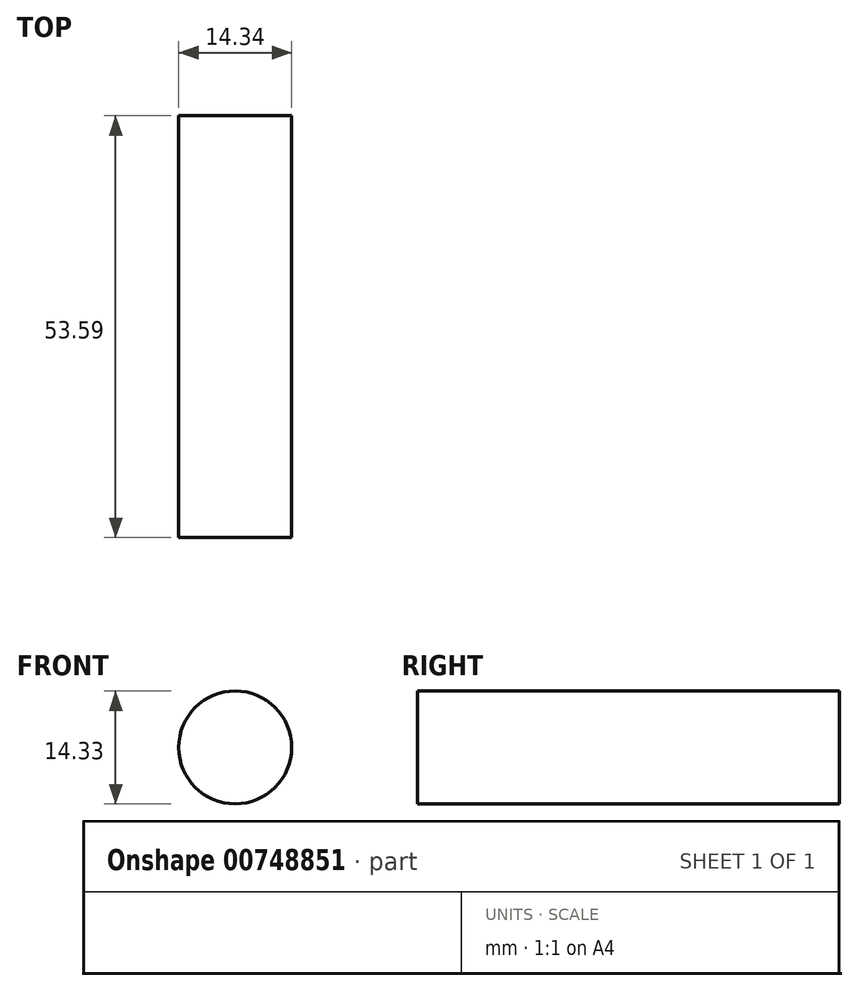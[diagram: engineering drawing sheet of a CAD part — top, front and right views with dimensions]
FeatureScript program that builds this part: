
annotation { "Feature Type Name" : "Feature", "Feature Type Description" : "" }
export const myFeature = defineFeature(function(context is Context, id is Id, definition is map)
    precondition{}
    {
        {
            var Q0;
            Q0=qCreatedBy(makeId("Front.planeOp"),FACE);
            var sketch = newSketch(context, id + "F0", { "sketchPlane" : qUnion([Q0])});
            skCircle(sketch, "E0", {"center": v(-17.36, 11.76) * mm, "radius": 7.17 * mm});
            skSolve(sketch);
        }
        {
            var Q0;
            Q0 = qSketchRegion(id + "F0", true);
            extrude(context, id + "F1", {"entities" : qUnion([Q0]), "depth" : 53.6 * mm, "offsetDistance" : 25.4 * mm});
        }
    });
